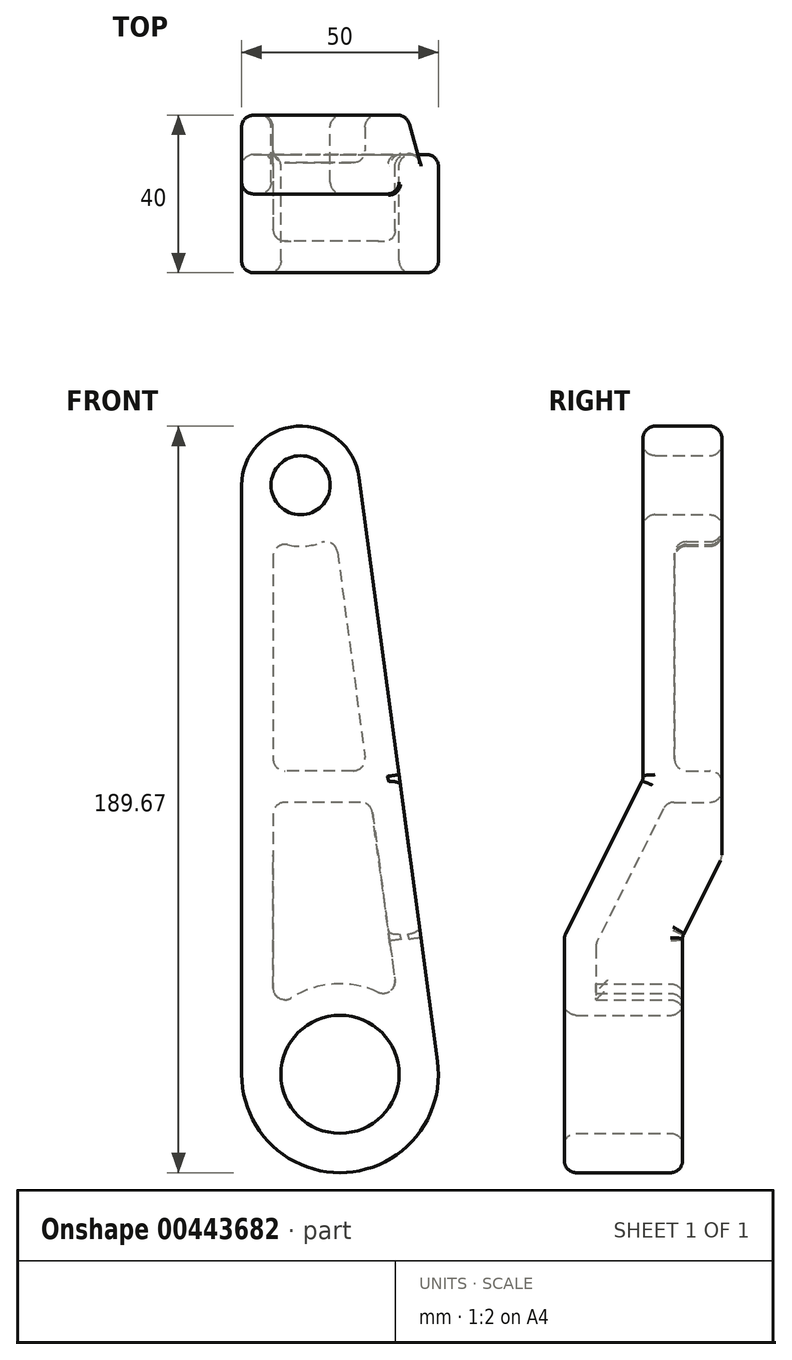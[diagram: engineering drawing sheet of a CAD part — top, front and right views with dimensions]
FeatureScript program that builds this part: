
annotation { "Feature Type Name" : "Feature", "Feature Type Description" : "" }
export const myFeature = defineFeature(function(context is Context, id is Id, definition is map)
    precondition{}
    {
        {
            var Q0;
            Q0=qCreatedBy(makeId("Front.planeOp"),FACE);
            var sketch = newSketch(context, id + "F0", { "sketchPlane" : qUnion([Q0])});
            skArc(sketch, "E0", {"start": v(-25, 0) * mm, "mid": v(1.67, -24.94) * mm, "end": v(24.78, 3.33) * mm});
            skArc(sketch, "E1", {"start": v(4.87, 151.66) * mm, "mid": v(-11, 164.63) * mm, "end": v(-25, 149.67) * mm});
            skLineSegment(sketch, "E2", {"start": v(-25, 149.67) * mm, "end": v(-25, 0) * mm});
            skLineSegment(sketch, "E3", {"start": v(4.87, 151.66) * mm, "end": v(24.78, 3.33) * mm});
            skSolve(sketch);
        }
        {
            var Q0;
            Q0=makeQuery(id+"F0.imprint","IMPRINT",FACE,{"disambiguationData":[TD([[makeQuery(id+"F0.imprint","IMPRINT",EDGE,{"derivedFrom":sQuery(id+"F0.wireOp",EDGE,"E0")}),1.0]])]});
            extrude(context, id + "F1", {"entities" : qUnion([Q0]), "depth" : 40 * mm});
        }
        {
            var Q0;
            Q0=makeQuery(id+"F1.opExtrude","SWEPT_FACE",FACE,{"disambiguationData":[OSD([sQuery(id+"F0.wireOp",EDGE,"E2")])]});
            var sketch = newSketch(context, id + "F2", { "sketchPlane" : qUnion([Q0])});
            skLineSegment(sketch, "E4", {"start": v(0, 0) * mm, "end": v(0, -25.94) * mm});
            skLineSegment(sketch, "E5", {"start": v(0, -25.94) * mm, "end": v(10, -25.94) * mm});
            skLineSegment(sketch, "E6", {"start": v(10, -25.94) * mm, "end": v(10, 35) * mm});
            skLineSegment(sketch, "E7", {"start": v(10, 35) * mm, "end": v(0, 55) * mm});
            skLineSegment(sketch, "E8", {"start": v(0, 55) * mm, "end": v(0, 0) * mm});
            skLineSegment(sketch, "E9", {"start": v(40, 35) * mm, "end": v(40, 149.67) * mm});
            skLineSegment(sketch, "E10", {"start": v(40, 149.67) * mm, "end": v(40, 165.63) * mm});
            skLineSegment(sketch, "E11", {"start": v(40, 165.63) * mm, "end": v(20, 165.63) * mm});
            skLineSegment(sketch, "E12", {"start": v(20, 165.63) * mm, "end": v(20, 75) * mm});
            skLineSegment(sketch, "E13", {"start": v(20, 75) * mm, "end": v(40, 35) * mm});
            skSolve(sketch);
        }
        {
            var Q0;
            {var subQ0=sQuery(id+"F2.wireOp",EDGE,"E9");Q0=makeQuery(id+"F2.imprint","IMPRINT",FACE,{"disambiguationData":[TD([[makeQuery(id+"F2.imprint","IMPRINT",EDGE,{"derivedFrom":subQ0}),-1.0]])]});}
            var Q1;
            {var subQ0=sQuery(id+"F2.wireOp",EDGE,"E10");Q1=makeQuery(id+"F2.imprint","IMPRINT",FACE,{"disambiguationData":[TD([[makeQuery(id+"F2.imprint","IMPRINT",EDGE,{"derivedFrom":subQ0}),1.0]])]});}
            var Q2;
            {var subQ0=sQuery(id+"F2.wireOp",EDGE,"E7");Q2=makeQuery(id+"F2.imprint","IMPRINT",FACE,{"disambiguationData":[TD([[makeQuery(id+"F2.imprint","IMPRINT",EDGE,{"derivedFrom":subQ0}),1.0]])]});}
            var Q3;
            {var subQ0=sQuery(id+"F2.wireOp",EDGE,"E4");Q3=makeQuery(id+"F2.imprint","IMPRINT",FACE,{"disambiguationData":[TD([[makeQuery(id+"F2.imprint","IMPRINT",EDGE,{"derivedFrom":subQ0}),1.0]])]});}
            extrude(context, id + "F3", {"entities" : qUnion([Q0, Q1, Q2, Q3]), "operationType" : NewBodyOperationType.REMOVE, "endBound" : BoundingType.THROUGH_ALL, "oppositeDirection" : true, "depth" : 25 * mm});
        }
        {
            var Q0;
            Q0=makeQuery(id+"F1.opExtrude","CAP_FACE",FACE,{"disambiguationData":[OSD([sQuery(id+"F0.wireOp",EDGE,"E0"),sQuery(id+"F0.wireOp",EDGE,"E1"),sQuery(id+"F0.wireOp",EDGE,"E2"),sQuery(id+"F0.wireOp",EDGE,"E3")])],"isStart":true});
            var sketch = newSketch(context, id + "F4", { "sketchPlane" : qUnion([Q0])});
            skCircle(sketch, "E14", {"center": v(10, 149.67) * mm, "radius": 7.5 * mm});
            skCircle(sketch, "E15", {"center": v(0, 0) * mm, "radius": 15 * mm});
            skSolve(sketch);
        }
        {
            var Q0;
            Q0 = qSketchRegion(id + "F4", true);
            extrude(context, id + "F5", {"entities" : qUnion([Q0]), "operationType" : NewBodyOperationType.REMOVE, "endBound" : BoundingType.THROUGH_ALL, "oppositeDirection" : true, "depth" : 25 * mm});
        }
        {
            var Q0;
            Q0=makeQuery(id+"F1.opExtrude","CAP_FACE",FACE,{"disambiguationData":[OSD([sQuery(id+"F0.wireOp",EDGE,"E0"),sQuery(id+"F0.wireOp",EDGE,"E1"),sQuery(id+"F0.wireOp",EDGE,"E2"),sQuery(id+"F0.wireOp",EDGE,"E3")])],"isStart":true});
            var Q1;
            Q1=makeQuery(id+"F3.boolean.opBoolean","COPY",FACE,{"derivedFrom":makeQuery(id+"F3.opExtrude","SWEPT_FACE",FACE,{"disambiguationData":[OSD([sQuery(id+"F2.wireOp",EDGE,"E7")])]})});
            var Q2;
            Q2=makeQuery(id+"F3.boolean.opBoolean","COPY",FACE,{"derivedFrom":makeQuery(id+"F3.opExtrude","SWEPT_FACE",FACE,{"disambiguationData":[OSD([sQuery(id+"F2.wireOp",EDGE,"E6")])]})});
            shell(context, id + "F6", {"entities" : qUnion([Q0, Q1, Q2]), "thickness" : 8 * mm});
        }
        {
            var Q0;
            Q0=makeQuery(id+"F1.opExtrude","CAP_FACE",FACE,{"disambiguationData":[OSD([sQuery(id+"F0.wireOp",EDGE,"E0"),sQuery(id+"F0.wireOp",EDGE,"E1"),sQuery(id+"F0.wireOp",EDGE,"E2"),sQuery(id+"F0.wireOp",EDGE,"E3")])],"isStart":true});
            var sketch = newSketch(context, id + "F7", { "sketchPlane" : qUnion([Q0])});
            skLineSegment(sketch, "E16", {"start": v(-6.8, 77.11) * mm, "end": v(17, 77.11) * mm});
            skLineSegment(sketch, "E17", {"start": v(-7.88, 69.11) * mm, "end": v(17, 69.11) * mm});
            skSolve(sketch);
        }
        {
            var Q0;
            {var subQ0=sQuery(id+"F7.wireOp",EDGE,"E16");Q0=makeQuery(id+"F7.imprint","IMPRINT",FACE,{"disambiguationData":[TD([[makeQuery(id+"F7.imprint","IMPRINT",EDGE,{"derivedFrom":subQ0}),-1.0]])]});}
            var Q1;
            Q1=makeQuery(id+"F1.opExtrude","SWEPT_BODY",BODY,{"disambiguationData":[OSD([sQuery(id+"F0.wireOp",EDGE,"E0"),sQuery(id+"F0.wireOp",EDGE,"E1"),sQuery(id+"F0.wireOp",EDGE,"E2"),sQuery(id+"F0.wireOp",EDGE,"E3")])]});
            extrude(context, id + "F8", {"entities" : qUnion([Q0]), "operationType" : NewBodyOperationType.ADD, "endBound" : BoundingType.UP_TO_NEXT, "oppositeDirection" : true, "endBoundEntityBody" : qUnion([Q1]), "depth" : 4 * mm});
        }
        {
            var Q0;
            Q0=makeQuery(id+"F6.opShell","OFFSET_FACE",FACE,{"disambiguationData":[OSD([sQuery(id+"F2.wireOp",EDGE,"E7")])]});
            var Q1;
            Q1=makeQuery(id+"F3.boolean.opBoolean","COPY",FACE,{"derivedFrom":makeQuery(id+"F3.opExtrude","SWEPT_FACE",FACE,{"disambiguationData":[OSD([sQuery(id+"F2.wireOp",EDGE,"E7")])]})});
            var Q2;
            Q2=makeQuery(id+"F6.opShell","OFFSET_FACE",FACE,{"disambiguationData":[OSD([sQuery(id+"F2.wireOp",EDGE,"E13")])]});
            var Q3;
            {var subQ1=sQuery(id+"F0.wireOp",EDGE,"E2");Q3=makeQuery(id+"F8.boolean.opBoolean","SPLIT",FACE,{"disambiguationData":[TD([makeQuery(id+"F3.boolean.opBoolean","COPY",FACE,{"derivedFrom":makeQuery(id+"F3.opExtrude","SWEPT_FACE",FACE,{"disambiguationData":[OSD([sQuery(id+"F2.wireOp",EDGE,"E6")])]})})])],"derivedFrom":makeQuery(id+"F6.opShell","OFFSET_FACE",FACE,{"disambiguationData":[OSD([subQ1])]})});}
            var Q4;
            {var subQ0=sQuery(id+"F0.wireOp",EDGE,"E3");Q4=makeQuery(id+"F8.boolean.opBoolean","SPLIT",FACE,{"disambiguationData":[TD([makeQuery(id+"F3.boolean.opBoolean","COPY",FACE,{"derivedFrom":makeQuery(id+"F3.opExtrude","SWEPT_FACE",FACE,{"disambiguationData":[OSD([sQuery(id+"F2.wireOp",EDGE,"E6")])]})})])],"derivedFrom":makeQuery(id+"F6.opShell","OFFSET_FACE",FACE,{"disambiguationData":[OSD([subQ0])]})});}
            var Q5;
            Q5=makeQuery(id+"F3.boolean.opBoolean","COPY",FACE,{"derivedFrom":makeQuery(id+"F3.opExtrude","SWEPT_FACE",FACE,{"disambiguationData":[OSD([sQuery(id+"F2.wireOp",EDGE,"E6")])]})});
            var Q6;
            Q6=makeQuery(id+"F3.boolean.opBoolean","COPY",FACE,{"derivedFrom":makeQuery(id+"F3.opExtrude","SWEPT_FACE",FACE,{"disambiguationData":[OSD([sQuery(id+"F2.wireOp",EDGE,"E13")])]})});
            var Q7;
            Q7=makeQuery(id+"F1.opExtrude","CAP_FACE",FACE,{"disambiguationData":[OSD([sQuery(id+"F0.wireOp",EDGE,"E0"),sQuery(id+"F0.wireOp",EDGE,"E1"),sQuery(id+"F0.wireOp",EDGE,"E2"),sQuery(id+"F0.wireOp",EDGE,"E3")])],"isStart":false});
            var Q8;
            {var subQ1=sQuery(id+"F0.wireOp",EDGE,"E3");Q8=makeQuery(id+"F8.boolean.opBoolean","SPLIT",FACE,{"disambiguationData":[TD([makeQuery(id+"F6.opShell","OFFSET_FACE",FACE,{"disambiguationData":[OSD([sQuery(id+"F4.wireOp",EDGE,"E14")])]})])],"derivedFrom":makeQuery(id+"F6.opShell","OFFSET_FACE",FACE,{"disambiguationData":[OSD([subQ1])]})});}
            var Q9;
            Q9=makeQuery(id+"F3.boolean.opBoolean","COPY",FACE,{"derivedFrom":makeQuery(id+"F3.opExtrude","SWEPT_FACE",FACE,{"disambiguationData":[OSD([sQuery(id+"F2.wireOp",EDGE,"E12")])]})});
            var Q10;
            Q10=makeQuery(id+"F5.boolean.opBoolean","COPY",FACE,{"derivedFrom":makeQuery(id+"F5.opExtrude","SWEPT_FACE",FACE,{"disambiguationData":[OSD([sQuery(id+"F4.wireOp",EDGE,"E14")])]})});
            var Q11;
            Q11=makeQuery(id+"F6.opShell","OFFSET_FACE",FACE,{"disambiguationData":[OSD([sQuery(id+"F2.wireOp",EDGE,"E12")])]});
            var Q12;
            Q12=makeQuery(id+"F6.opShell","OFFSET_FACE",FACE,{"disambiguationData":[OSD([sQuery(id+"F4.wireOp",EDGE,"E14")])]});
            var Q13;
            Q13=makeQuery(id+"F8.opExtrude","CAP_EDGE",EDGE,{"disambiguationData":[OSD([sQuery(id+"F7.wireOp",EDGE,"E16")])],"isStart":true});
            var Q14;
            Q14=makeQuery(id+"F1.opExtrude","SWEPT_FACE",FACE,{"disambiguationData":[OSD([sQuery(id+"F0.wireOp",EDGE,"E3")])]});
            var Q15;
            Q15=makeQuery(id+"F1.opExtrude","CAP_EDGE",EDGE,{"disambiguationData":[OSD([sQuery(id+"F0.wireOp",EDGE,"E3")])],"isStart":true});
            var Q16;
            {var subQ0=sQuery(id+"F0.wireOp",EDGE,"E2");Q16=makeQuery(id+"F8.boolean.opBoolean","SPLIT",EDGE,{"disambiguationData":[TD([makeQuery(id+"F3.boolean.opBoolean","COPY",FACE,{"derivedFrom":makeQuery(id+"F3.opExtrude","SWEPT_FACE",FACE,{"disambiguationData":[OSD([sQuery(id+"F2.wireOp",EDGE,"E7")])]})})])],"derivedFrom":makeQuery(id+"F6.opShell","OFFSET_EDGE",EDGE,{"disambiguationData":[OSD([subQ0]),TDD([makeQuery(id+"F1.opExtrude","CAP_EDGE",EDGE,{"disambiguationData":[OSD([subQ0])],"isStart":true})])]})});}
            var Q17;
            Q17=makeQuery(id+"F1.opExtrude","CAP_EDGE",EDGE,{"disambiguationData":[OSD([sQuery(id+"F0.wireOp",EDGE,"E2")])],"isStart":true});
            var Q18;
            Q18=makeQuery(id+"F8.opExtrude","CAP_EDGE",EDGE,{"disambiguationData":[OSD([sQuery(id+"F7.wireOp",EDGE,"E17")])],"isStart":true});
            var Q19;
            {var subQ2=sQuery(id+"F0.wireOp",EDGE,"E2");Q19=makeQuery(id+"F8.boolean.opBoolean","SPLIT",EDGE,{"disambiguationData":[TD([makeQuery(id+"F6.opShell","OFFSET_FACE",FACE,{"disambiguationData":[OSD([sQuery(id+"F4.wireOp",EDGE,"E14")])]})])],"derivedFrom":makeQuery(id+"F6.opShell","OFFSET_EDGE",EDGE,{"disambiguationData":[OSD([subQ2]),TDD([makeQuery(id+"F1.opExtrude","CAP_EDGE",EDGE,{"disambiguationData":[OSD([subQ2])],"isStart":true})])]})});}
            var Q20;
            Q20=makeQuery(id+"F1.opExtrude","CAP_EDGE",EDGE,{"disambiguationData":[OSD([sQuery(id+"F0.wireOp",EDGE,"E1")])],"isStart":true});
            var Q21;
            Q21=makeQuery(id+"F8.opExtrude","SWEPT_EDGE",EDGE,{"disambiguationData":[OSD([sQuery(id+"F0.wireOp",EDGE,"E2"),sQuery(id+"F7.wireOp",EDGE,"E16")])]});
            fillet(context, id + "F9", {"entities" : qUnion([Q0, Q1, Q2, Q3, Q4, Q5, Q6, Q7, Q8, Q9, Q10, Q11, Q12, Q13, Q14, Q15, Q16, Q17, Q18, Q19, Q20, Q21]), "radius" : 3 * mm, "tangentPropagation" : true, "allowEdgeOverflow" : false});
        }
    });
